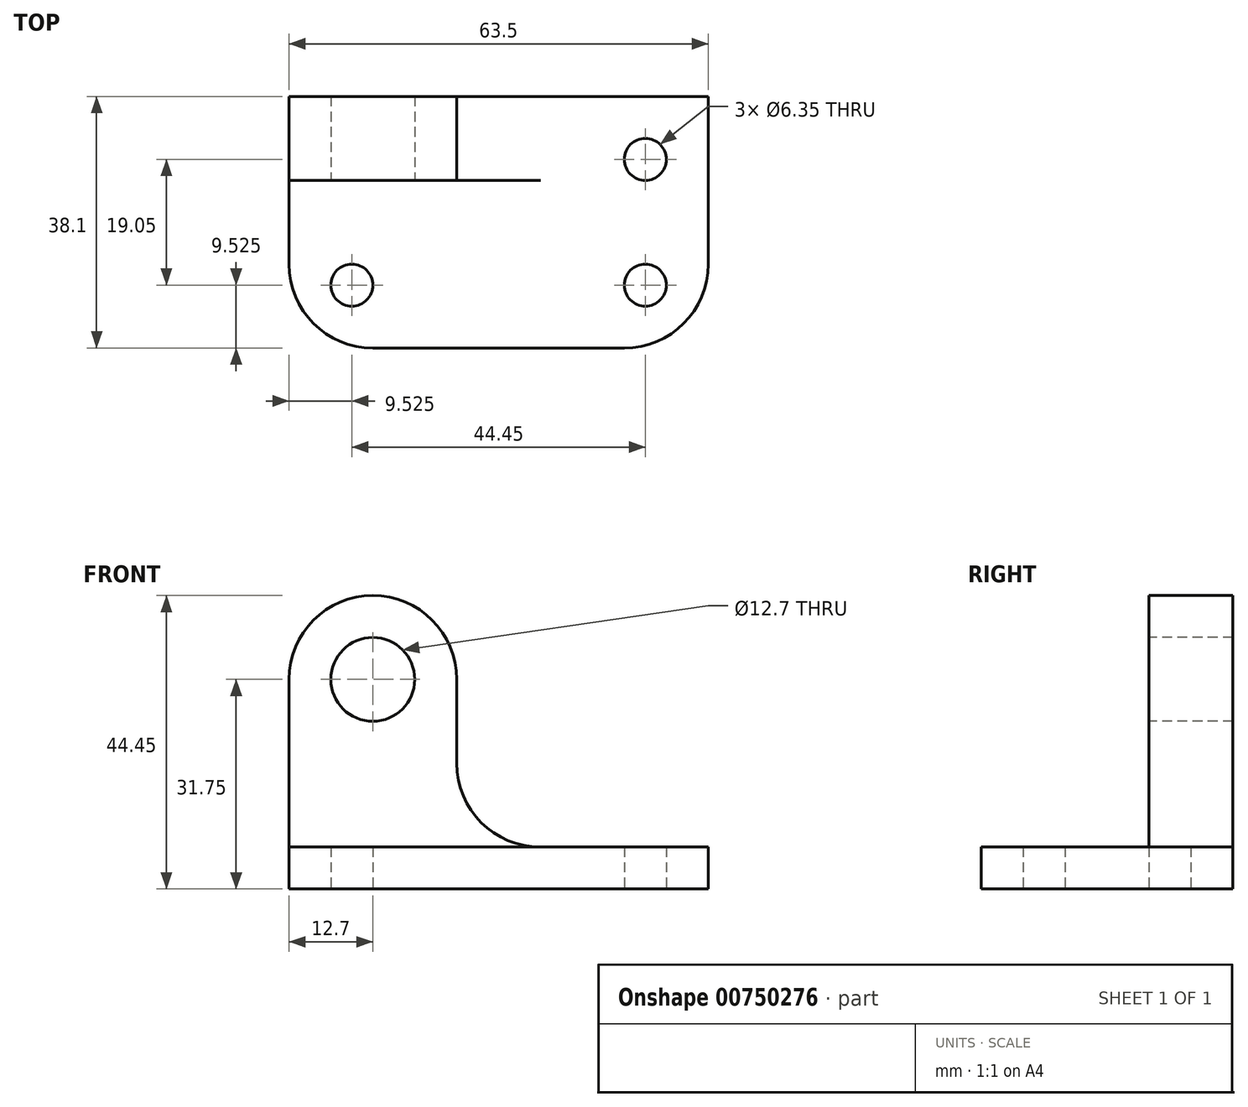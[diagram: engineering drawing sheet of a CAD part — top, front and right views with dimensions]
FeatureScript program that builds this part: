
annotation { "Feature Type Name" : "Feature", "Feature Type Description" : "" }
export const myFeature = defineFeature(function(context is Context, id is Id, definition is map)
    precondition{}
    {
        {
            var Q0;
            Q0=qCreatedBy(makeId("Top.planeOp"),FACE);
            var sketch = newSketch(context, id + "F0", { "sketchPlane" : qUnion([Q0])});
            skLineSegment(sketch, "E0", {"start": v(0, 12.7) * mm, "end": v(12.7, 12.7) * mm});
            skLineSegment(sketch, "E1", {"start": v(12.7, 12.7) * mm, "end": v(12.7, 0) * mm});
            skLineSegment(sketch, "E2", {"start": v(12.7, 0) * mm, "end": v(50.8, 0) * mm});
            skLineSegment(sketch, "E3", {"start": v(50.8, 0) * mm, "end": v(50.8, 12.7) * mm});
            skLineSegment(sketch, "E4", {"start": v(50.8, 12.7) * mm, "end": v(63.5, 12.7) * mm});
            skLineSegment(sketch, "E5", {"start": v(63.5, 12.7) * mm, "end": v(63.5, 38.1) * mm});
            skLineSegment(sketch, "E6", {"start": v(63.5, 38.1) * mm, "end": v(0, 38.1) * mm});
            skLineSegment(sketch, "E7", {"start": v(0, 38.1) * mm, "end": v(0, 12.7) * mm});
            skArc(sketch, "E8", {"start": v(0, 12.7) * mm, "mid": v(3.72, 3.72) * mm, "end": v(12.7, 0) * mm});
            skArc(sketch, "E9", {"start": v(50.8, 0) * mm, "mid": v(59.78, 3.72) * mm, "end": v(63.5, 12.7) * mm});
            skCircle(sketch, "E10", {"center": v(53.98, 28.58) * mm, "radius": 3.18 * mm});
            skCircle(sketch, "E11", {"center": v(9.53, 9.53) * mm, "radius": 3.18 * mm});
            skCircle(sketch, "E12", {"center": v(53.98, 9.53) * mm, "radius": 3.18 * mm});
            skLineSegment(sketch, "E13.bottom", {"start": v(0, 25.4) * mm, "end": v(25.4, 25.4) * mm});
            skLineSegment(sketch, "E13.top", {"start": v(0, 38.1) * mm, "end": v(25.4, 38.1) * mm});
            skLineSegment(sketch, "E13.left", {"start": v(0, 25.4) * mm, "end": v(0, 38.1) * mm});
            skLineSegment(sketch, "E13.right", {"start": v(25.4, 25.4) * mm, "end": v(25.4, 38.1) * mm});
            skSolve(sketch);
        }
        {
            var Q0;
            {var subQ9=sQuery(id+"F0.wireOp",EDGE,"E2");Q0=makeQuery(id+"F0.imprint","IMPRINT",FACE,{"disambiguationData":[TD([[makeQuery(id+"F0.imprint","IMPRINT",EDGE,{"derivedFrom":subQ9}),1.0]])]});}
            var Q1;
            {var subQ0=sQuery(id+"F0.wireOp",EDGE,"E9");Q1=makeQuery(id+"F0.imprint","IMPRINT",FACE,{"disambiguationData":[TD([[makeQuery(id+"F0.imprint","IMPRINT",EDGE,{"derivedFrom":subQ0}),1.0]])]});}
            var Q2;
            {var subQ0=sQuery(id+"F0.wireOp",EDGE,"E8");Q2=makeQuery(id+"F0.imprint","IMPRINT",FACE,{"disambiguationData":[TD([[makeQuery(id+"F0.imprint","IMPRINT",EDGE,{"derivedFrom":subQ0}),1.0]])]});}
            extrude(context, id + "F1", {"entities" : qUnion([Q0, Q1, Q2]), "depth" : 6.35 * mm, "offsetDistance" : 25.4 * mm});
        }
        {
            var Q0;
            Q0=makeQuery(id+"F0.imprint","IMPRINT",FACE,{"disambiguationData":[TD([[makeQuery(id+"F0.imprint","IMPRINT",EDGE,{"derivedFrom":sQuery(id+"F0.wireOp",EDGE,"E13.bottom")}),1.0]])]});
            extrude(context, id + "F2", {"entities" : qUnion([Q0]), "operationType" : NewBodyOperationType.ADD, "depth" : 31.75 * mm, "offsetDistance" : 25.4 * mm});
        }
        {
            var Q0;
            Q0=makeQuery(id+"F2.opExtrude","SWEPT_FACE",FACE,{"disambiguationData":[OSD([sQuery(id+"F0.wireOp",EDGE,"E13.bottom")])]});
            var sketch = newSketch(context, id + "F3", { "sketchPlane" : qUnion([Q0])});
            skArc(sketch, "E14", {"start": v(25.4, 31.75) * mm, "mid": v(12.7, 44.45) * mm, "end": v(0, 31.75) * mm});
            skCircle(sketch, "E15", {"center": v(12.7, 31.75) * mm, "radius": 6.35 * mm});
            skLineSegment(sketch, "E16", {"start": v(25.4, 6.35) * mm, "end": v(25.4, 19.05) * mm});
            skLineSegment(sketch, "E17", {"start": v(25.4, 19.05) * mm, "end": v(38.1, 19.05) * mm});
            skLineSegment(sketch, "E18", {"start": v(38.1, 19.05) * mm, "end": v(38.1, 6.35) * mm});
            skLineSegment(sketch, "E19", {"start": v(38.1, 6.35) * mm, "end": v(25.4, 6.35) * mm});
            skArc(sketch, "E20", {"start": v(25.4, 19.05) * mm, "mid": v(29.12, 10.07) * mm, "end": v(38.1, 6.35) * mm});
            skSolve(sketch);
        }
        {
            var Q0;
            Q0=makeQuery(id+"F3.imprint","IMPRINT",FACE,{"disambiguationData":[TD([[makeQuery(id+"F3.imprint","IMPRINT",EDGE,{"derivedFrom":sQuery(id+"F3.wireOp",EDGE,"E16")}),1.0]])]});
            extrude(context, id + "F4", {"entities" : qUnion([Q0]), "operationType" : NewBodyOperationType.ADD, "oppositeDirection" : true, "depth" : 12.7 * mm, "offsetDistance" : 25.4 * mm});
        }
        {
            var Q0;
            {var subQ0=sQuery(id+"F3.wireOp",EDGE,"E15");var subQ1=makeQuery(id+"F2.opExtrude","CAP_EDGE",EDGE,{"disambiguationData":[OSD([sQuery(id+"F0.wireOp",EDGE,"E13.bottom")])],"isStart":false});var subQ2=makeQuery(id+"F3.imprint","INTERSECT",VERTEX,{"disambiguationData":[OD(0.0)],"derivedFrom":[subQ1,subQ0]});Q0=makeQuery(id+"F3.imprint","IMPRINT",FACE,{"disambiguationData":[TD([[makeQuery(id+"F3.imprint","IMPRINT",EDGE,{"disambiguationData":[TD([[subQ2,1.0]])],"derivedFrom":subQ0}),1.0]])]});}
            var Q1;
            {var subQ0=sQuery(id+"F3.wireOp",EDGE,"E15");var subQ1=makeQuery(id+"F2.opExtrude","CAP_EDGE",EDGE,{"disambiguationData":[OSD([sQuery(id+"F0.wireOp",EDGE,"E13.bottom")])],"isStart":false});var subQ2=makeQuery(id+"F3.imprint","INTERSECT",VERTEX,{"disambiguationData":[OD(0.0)],"derivedFrom":[subQ1,subQ0]});Q1=makeQuery(id+"F3.imprint","IMPRINT",FACE,{"disambiguationData":[TD([[makeQuery(id+"F3.imprint","IMPRINT",EDGE,{"disambiguationData":[TD([[subQ2,-1.0]])],"derivedFrom":subQ0}),1.0]])]});}
            extrude(context, id + "F5", {"entities" : qUnion([Q0, Q1]), "operationType" : NewBodyOperationType.REMOVE, "oppositeDirection" : true, "depth" : 12.7 * mm, "offsetDistance" : 25.4 * mm});
        }
        {
            var Q0;
            {var subQ0=sQuery(id+"F3.wireOp",EDGE,"E14");Q0=makeQuery(id+"F3.imprint","IMPRINT",FACE,{"disambiguationData":[TD([[makeQuery(id+"F3.imprint","IMPRINT",EDGE,{"derivedFrom":subQ0}),1.0]])]});}
            extrude(context, id + "F6", {"entities" : qUnion([Q0]), "operationType" : NewBodyOperationType.ADD, "oppositeDirection" : true, "depth" : 12.7 * mm, "offsetDistance" : 25.4 * mm});
        }
        {
            var Q0;
            {var subQ0=sQuery(id+"F0.wireOp",EDGE,"E1");var subQ1=sQuery(id+"F0.wireOp",EDGE,"E0");var subQ2=makeQuery(id+"F0.imprint","INTERSECT",VERTEX,{"derivedFrom":[subQ1,subQ0]});Q0=makeQuery(id+"F0.imprint","IMPRINT",FACE,{"disambiguationData":[TD([[makeQuery(id+"F0.imprint","IMPRINT",EDGE,{"disambiguationData":[TD([[subQ2,1.0]])],"derivedFrom":subQ1}),-1.0]])]});}
            var Q1;
            {var subQ0=sQuery(id+"F0.wireOp",EDGE,"E4");var subQ1=sQuery(id+"F0.wireOp",EDGE,"E3");var subQ2=makeQuery(id+"F0.imprint","INTERSECT",VERTEX,{"derivedFrom":[subQ1,subQ0]});Q1=makeQuery(id+"F0.imprint","IMPRINT",FACE,{"disambiguationData":[TD([[makeQuery(id+"F0.imprint","IMPRINT",EDGE,{"disambiguationData":[TD([[subQ2,1.0]])],"derivedFrom":subQ1}),-1.0]])]});}
            extrude(context, id + "F7", {"entities" : qUnion([Q0, Q1]), "operationType" : NewBodyOperationType.ADD, "depth" : 6.35 * mm, "offsetDistance" : 25.4 * mm});
        }
    });
